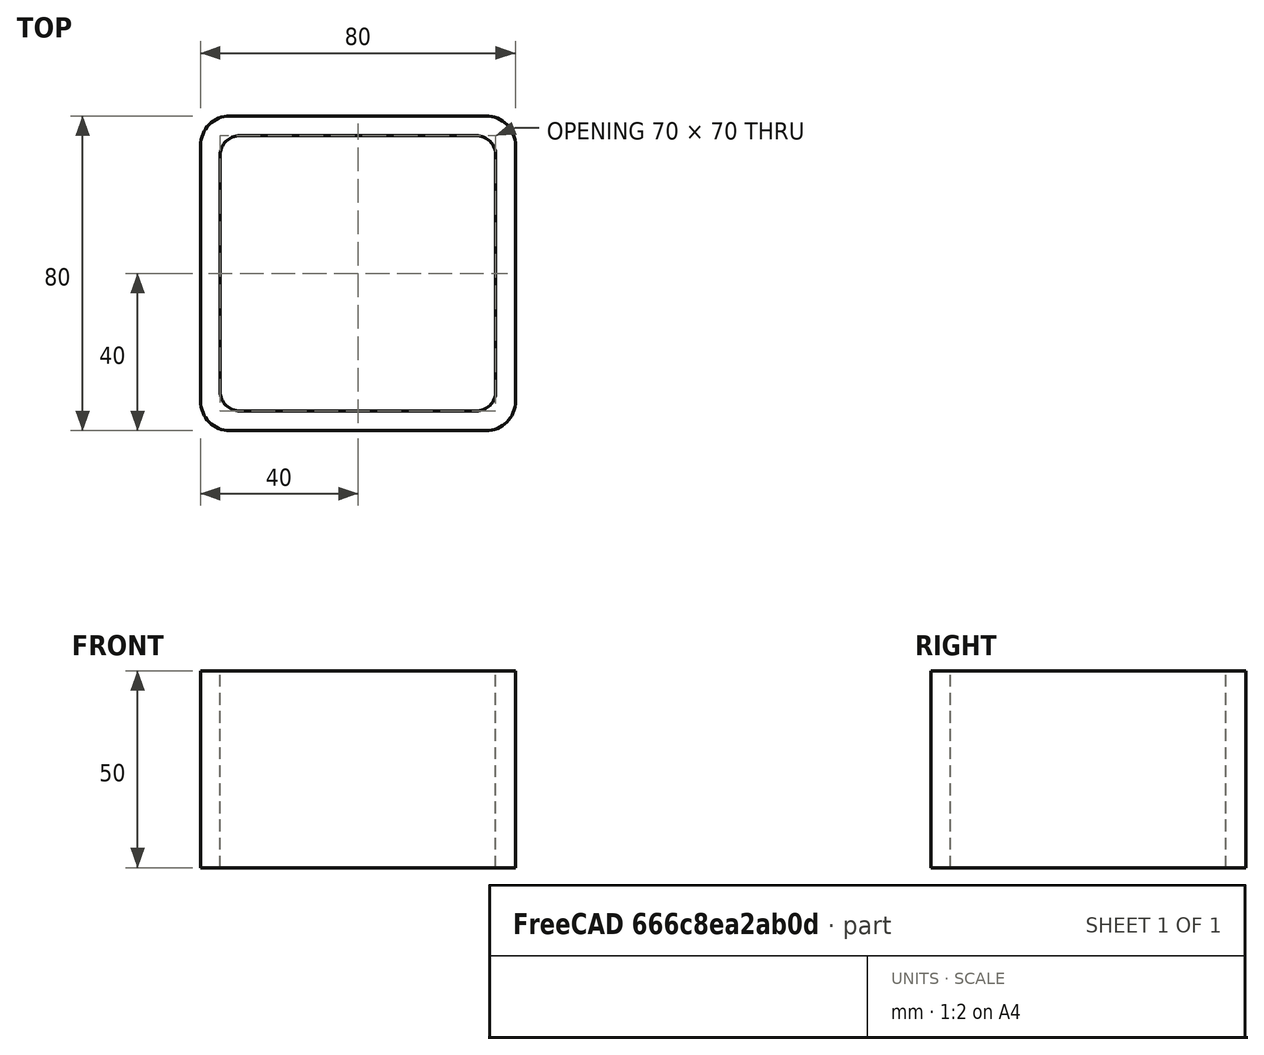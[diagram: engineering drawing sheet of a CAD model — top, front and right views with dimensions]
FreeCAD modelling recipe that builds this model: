
FCSTD DOCUMENT  (FreeCAD 0.15R4671 (Git))
Label: Square hollow section 80x80x5 EN10219 S235JRH
License: All rights reserved
LicenseURL: http://en.wikipedia.org/wiki/All_rights_reserved
objects: Sketcher::SketchObject×1, Part::Extrusion×1
note: 2 computed .brp shape members not serialized (recipe doc carries the construction recipe); baked Part::Feature solids carry a one-line shape summary decoded from their .brp

FEATURE [Sketcher::SketchObject] Sketch
  sketch-geometry (16):
    g0: LineSegment StartX=-30 StartY=35 StartZ=0 EndX=30 EndY=35 EndZ=0
    g1: LineSegment StartX=35 StartY=30 StartZ=0 EndX=35 EndY=-30 EndZ=0
    g2: LineSegment StartX=30 StartY=-35 StartZ=0 EndX=-30 EndY=-35 EndZ=0
    g3: LineSegment StartX=-35 StartY=-30 StartZ=0 EndX=-35 EndY=30 EndZ=0
    g4: LineSegment StartX=-32.5 StartY=40 StartZ=0 EndX=32.5 EndY=40 EndZ=0
    g5: LineSegment StartX=40 StartY=32.5 StartZ=0 EndX=40 EndY=-32.5 EndZ=0
    g6: LineSegment StartX=32.5 StartY=-40 StartZ=0 EndX=-32.5 EndY=-40 EndZ=0
    g7: LineSegment StartX=-40 StartY=-32.5 StartZ=0 EndX=-40 EndY=32.5 EndZ=0
    g8: ArcOfCircle CenterX=-30 CenterY=30 CenterZ=0 NormalX=0 NormalY=0 NormalZ=1 Radius=5 StartAngle=1.5708 EndAngle=3.14159
    g9: ArcOfCircle CenterX=30 CenterY=30 CenterZ=0 NormalX=0 NormalY=0 NormalZ=1 Radius=5 StartAngle=0 EndAngle=1.5708
    g10: ArcOfCircle CenterX=30 CenterY=-30 CenterZ=0 NormalX=0 NormalY=0 NormalZ=1 Radius=5 StartAngle=4.71239 EndAngle=6.28319
    g11: ArcOfCircle CenterX=-30 CenterY=-30 CenterZ=0 NormalX=0 NormalY=0 NormalZ=1 Radius=5 StartAngle=3.14159 EndAngle=4.71239
    g12: ArcOfCircle CenterX=32.5 CenterY=32.5 CenterZ=0 NormalX=0 NormalY=0 NormalZ=1 Radius=7.5 StartAngle=0 EndAngle=1.5708
    g13: ArcOfCircle CenterX=32.5 CenterY=-32.5 CenterZ=0 NormalX=0 NormalY=0 NormalZ=1 Radius=7.5 StartAngle=4.71239 EndAngle=6.28319
    g14: ArcOfCircle CenterX=-32.5 CenterY=-32.5 CenterZ=0 NormalX=0 NormalY=0 NormalZ=1 Radius=7.5 StartAngle=3.14159 EndAngle=4.71239
    g15: ArcOfCircle CenterX=-32.5 CenterY=32.5 CenterZ=0 NormalX=0 NormalY=0 NormalZ=1 Radius=7.5 StartAngle=1.5708 EndAngle=3.14159
  constraints (36):
    c: Horizontal(g2)
    c: Vertical(g3)
    c: Horizontal(g6)
    c: Vertical(g7)
    c: Tangent(g3,g8) = 1.5708
    c: Tangent(g0,g8) = 1.5708
    c: Tangent(g0,g9) = 1.5708
    c: Tangent(g1,g9) = 1.5708
    c: Tangent(g1,g10) = 1.5708
    c: Tangent(g2,g10) = 1.5708
    c: Tangent(g2,g11) = 1.5708
    c: Tangent(g3,g11) = 1.5708
    c: Tangent(g4,g12) = 1.5708
    c: Tangent(g5,g12) = 1.5708
    c: Tangent(g5,g13) = 1.5708
    c: Tangent(g6,g13) = 1.5708
    c: Tangent(g6,g14) = 1.5708
    c: Tangent(g7,g14) = 1.5708
    c: Tangent(g7,g15) = 1.5708
    c: Tangent(g4,g15) = 1.5708
    c: Equal(g9,g8)
    c: Equal(g9,g11)
    c: Equal(g9,g10)
    c: Equal(g12,g15)
    c: Equal(g12,g14)
    c: Equal(g12,g13)
    c: Symmetric(g4,g6,g-1)
    c: Symmetric(g7,g5,g-2)
    c: DistanceY(g4,g6) = -80
    c: DistanceX(g7,g5) = 80
    c: Symmetric(g3,g1,g-2)
    c: Symmetric(g0,g2,g-1)
    c: DistanceY(g0,g4) = 5
    c: DistanceX(g5,g1) = -5
    c: Radius(g9) = 5
    c: Radius(g12) = 7.5
FEATURE [Part::Extrusion] Extrude  label="Square hollow section 80x80x5 EN10219 S235JRH"
  Base = -> Sketch
  Dir = (0,0,50)
  Solid = true
